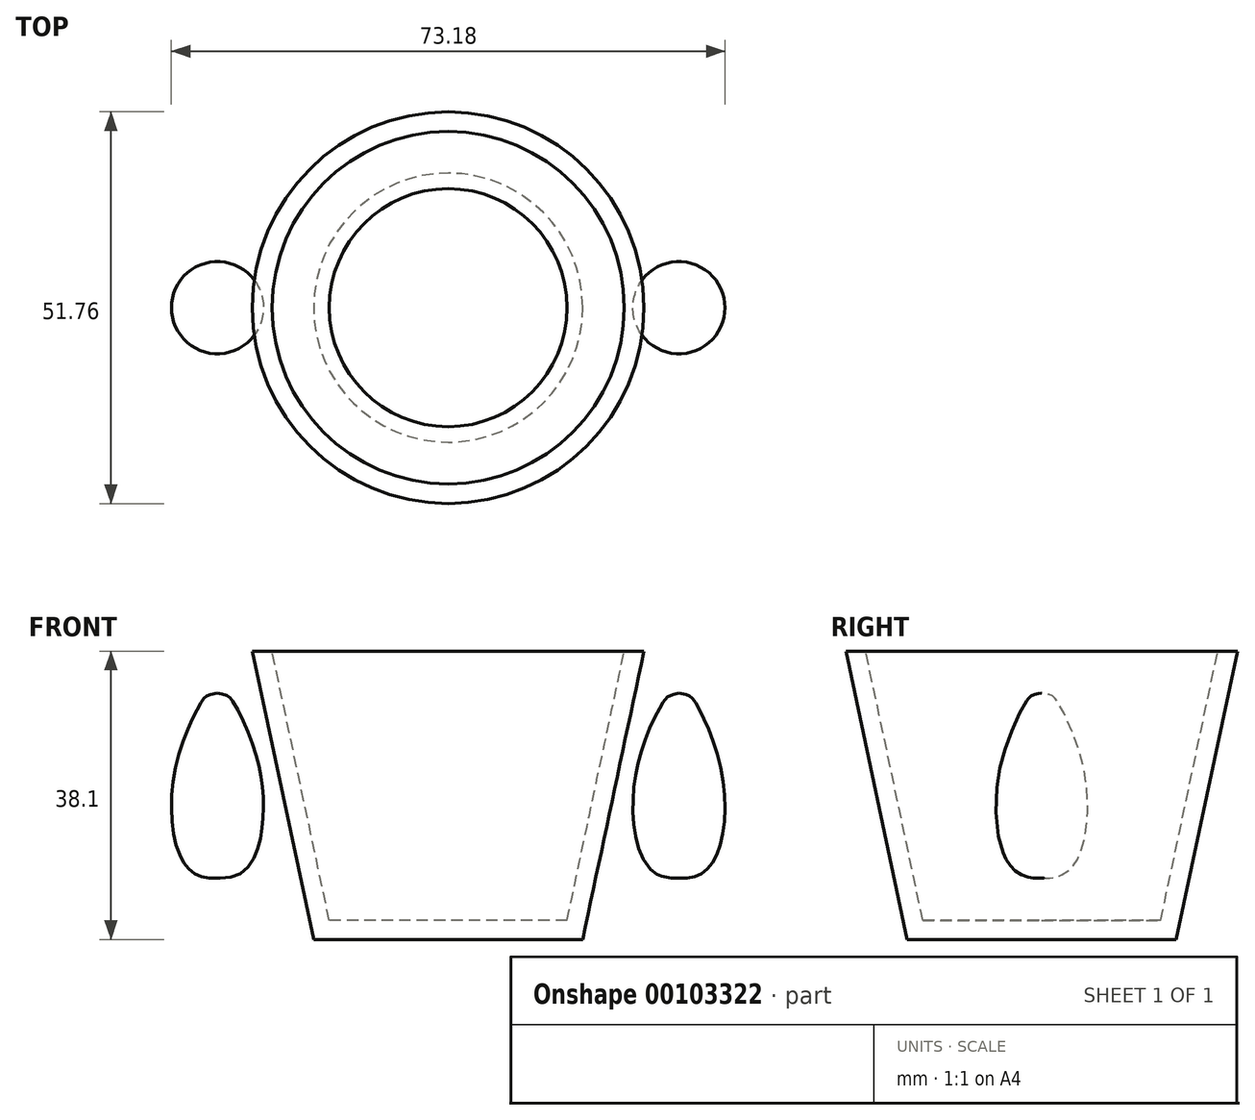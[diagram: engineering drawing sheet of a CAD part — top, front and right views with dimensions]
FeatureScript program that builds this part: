
annotation { "Feature Type Name" : "Feature", "Feature Type Description" : "" }
export const myFeature = defineFeature(function(context is Context, id is Id, definition is map)
    precondition{}
    {
        {
            var Q0;
            Q0=qCreatedBy(makeId("Top.planeOp"),FACE);
            var sketch = newSketch(context, id + "F0", { "sketchPlane" : qUnion([Q0])});
            skCircle(sketch, "E0", {"center": v(0, 0) * mm, "radius": 17.78 * mm});
            skSolve(sketch);
        }
        {
            var Q0;
            Q0=makeQuery(id+"F0.imprint","IMPRINT",FACE,{"disambiguationData":[TD([[makeQuery(id+"F0.imprint","IMPRINT",EDGE,{"derivedFrom":sQuery(id+"F0.wireOp",EDGE,"E0")}),1.0]])]});
            extrude(context, id + "F1", {"entities" : qUnion([Q0]), "depth" : 38.1 * mm, "hasDraft" : true, "draftAngle" : 12 * degree});
        }
        {
            var Q0;
            Q0=makeQuery(id+"F1.opExtrude","CAP_FACE",FACE,{"disambiguationData":[OSD([sQuery(id+"F0.wireOp",EDGE,"E0")])],"isStart":false});
            shell(context, id + "F2", {"entities" : qUnion([Q0]), "thickness" : 2.54 * mm});
        }
        {
            var Q0;
            Q0=qCreatedBy(makeId("Front.planeOp"),FACE);
            var sketch = newSketch(context, id + "F3", { "sketchPlane" : qUnion([Q0])});
            skLineSegment(sketch, "E1", {"start": v(-30.54, 40.74) * mm, "end": v(-30.41, -44.38) * mm});
            skFitSpline(sketch, "E2", {"points": [v(-30.54, 40.74) * mm, v(-32.92, 39.72) * mm, v(-38.04, 26.83) * mm, v(-36.34, 10.67) * mm, v(-30.49, 8.08) * mm, v(-19.09, 1.27) * mm], "startDerivative": vector(-47.7, -11.92) * mm, "endDerivative": vector(35.05, -111.41) * mm});
            skSolve(sketch);
        }
        {
            var Q0;
            {var subQ0=sQuery(id+"F3.wireOp",EDGE,"E2");Q0=makeQuery(id+"F3.imprint","IMPRINT",FACE,{"disambiguationData":[TD([[makeQuery(id+"F3.imprint","IMPRINT",EDGE,{"derivedFrom":subQ0}),1.0]])]});}
            var Q1;
            Q1=sQuery(id+"F3.wireOp",EDGE,"E1");
            revolve(context, id + "F4", {"entities" : qUnion([Q0]), "axis" : qUnion([Q1]), "revolveType" : RevolveType.FULL});
        }
        {
            var Q0;
            Q0=makeQuery(id+"F4.opRevolve","SWEPT_BODY",BODY,{"disambiguationData":[OSD([sQuery(id+"F3.wireOp",EDGE,"E1"),sQuery(id+"F3.wireOp",EDGE,"E2")])]});
            var Q1;
            {var subQ0=sQuery(id+"F3.wireOp",EDGE,"E2");var subQ1=sQuery(id+"F3.wireOp",EDGE,"E1");Q1=makeQuery(id+"F4.opRevolve","SWEPT_VERTEX",VERTEX,{"disambiguationData":[OSD([subQ1,subQ0]),TDD([makeQuery(id+"F3.imprint","INTERSECT",VERTEX,{"disambiguationData":[OD(0.0)],"derivedFrom":[subQ1,subQ0]})])]});}
            transform(context, id + "F5", {"entities" : qUnion([Q0]), "transformType" : TransformType.SCALE_UNIFORMLY, "scale" : .75, "scalePoint" : qUnion([Q1]), "makeCopy" : false});
        }
        {
            var Q0;
            Q0=qCreatedBy(makeId("Front.planeOp"),FACE);
            var sketch = newSketch(context, id + "F6", { "sketchPlane" : qUnion([Q0])});
            skLineSegment(sketch, "E3", {"start": v(0, -20.63) * mm, "end": v(0, 53.72) * mm});
            skSolve(sketch);
        }
        {
            var Q0;
            Q0=makeQuery(id+"F4.opRevolve","SWEPT_BODY",BODY,{"disambiguationData":[OSD([sQuery(id+"F3.wireOp",EDGE,"E1"),sQuery(id+"F3.wireOp",EDGE,"E2")])]});
            var Q1;
            Q1=sQuery(id+"F6.wireOp",EDGE,"E3");
            transform(context, id + "F7", {"entities" : qUnion([Q0]), "transformType" : TransformType.ROTATION, "transformAxis" : qUnion([Q1]), "angle" : 180 * degree, "makeCopy" : true});
        }
    });
